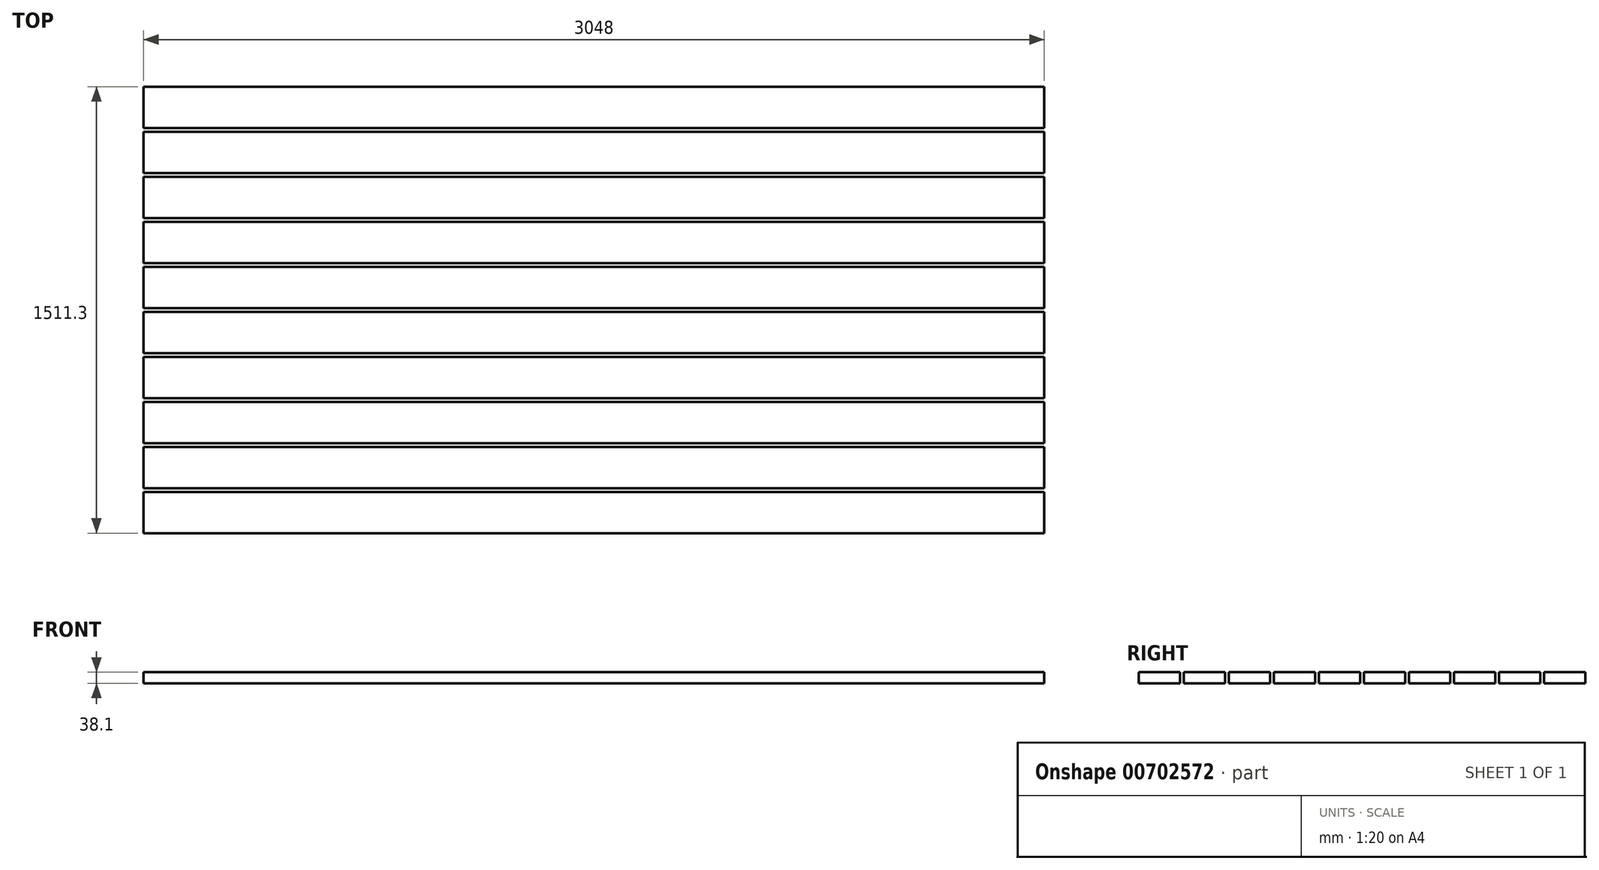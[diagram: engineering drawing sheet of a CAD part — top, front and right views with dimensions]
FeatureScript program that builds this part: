
annotation { "Feature Type Name" : "Feature", "Feature Type Description" : "" }
export const myFeature = defineFeature(function(context is Context, id is Id, definition is map)
    precondition{}
    {
        {
            var Q0;
            Q0=qCreatedBy(makeId("Top.planeOp"),FACE);
            var sketch = newSketch(context, id + "F0", { "sketchPlane" : qUnion([Q0])});
            skLineSegment(sketch, "E0.bottom", {"start": v(1524, 69.85) * mm, "end": v(-1524, 69.85) * mm});
            skLineSegment(sketch, "E0.top", {"start": v(1524, -69.85) * mm, "end": v(-1524, -69.85) * mm});
            skLineSegment(sketch, "E0.left", {"start": v(1524, 69.85) * mm, "end": v(1524, -69.85) * mm});
            skLineSegment(sketch, "E0.right", {"start": v(-1524, 69.85) * mm, "end": v(-1524, -69.85) * mm});
            skPoint(sketch, "E0.middle", {"position": v(0, 0) * mm});
            skLineSegment(sketch, "E1.bottom", {"start": v(-1524, -82.55) * mm, "end": v(1524, -82.55) * mm});
            skLineSegment(sketch, "E1.top", {"start": v(-1524, -222.25) * mm, "end": v(1524, -222.25) * mm});
            skLineSegment(sketch, "E1.left", {"start": v(-1524, -82.55) * mm, "end": v(-1524, -222.25) * mm});
            skLineSegment(sketch, "E1.right", {"start": v(1524, -82.55) * mm, "end": v(1524, -222.25) * mm});
            skLineSegment(sketch, "E2.bottom", {"start": v(-1524, -234.95) * mm, "end": v(1524, -234.95) * mm});
            skLineSegment(sketch, "E2.top", {"start": v(-1524, -374.65) * mm, "end": v(1524, -374.65) * mm});
            skLineSegment(sketch, "E2.left", {"start": v(-1524, -234.95) * mm, "end": v(-1524, -374.65) * mm});
            skLineSegment(sketch, "E2.right", {"start": v(1524, -234.95) * mm, "end": v(1524, -374.65) * mm});
            skLineSegment(sketch, "E3.bottom", {"start": v(-1524, -387.35) * mm, "end": v(1524, -387.35) * mm});
            skLineSegment(sketch, "E3.top", {"start": v(-1524, -527.05) * mm, "end": v(1524, -527.05) * mm});
            skLineSegment(sketch, "E3.left", {"start": v(-1524, -387.35) * mm, "end": v(-1524, -527.05) * mm});
            skLineSegment(sketch, "E3.right", {"start": v(1524, -387.35) * mm, "end": v(1524, -527.05) * mm});
            skLineSegment(sketch, "E4.bottom", {"start": v(-1524, -539.75) * mm, "end": v(1524, -539.75) * mm});
            skLineSegment(sketch, "E4.top", {"start": v(-1524, -679.45) * mm, "end": v(1524, -679.45) * mm});
            skLineSegment(sketch, "E4.left", {"start": v(-1524, -539.75) * mm, "end": v(-1524, -679.45) * mm});
            skLineSegment(sketch, "E4.right", {"start": v(1524, -539.75) * mm, "end": v(1524, -679.45) * mm});
            skLineSegment(sketch, "E5.bottom", {"start": v(-1524, -692.15) * mm, "end": v(1524, -692.15) * mm});
            skLineSegment(sketch, "E5.top", {"start": v(-1524, -831.85) * mm, "end": v(1524, -831.85) * mm});
            skLineSegment(sketch, "E5.left", {"start": v(-1524, -692.15) * mm, "end": v(-1524, -831.85) * mm});
            skLineSegment(sketch, "E5.right", {"start": v(1524, -692.15) * mm, "end": v(1524, -831.85) * mm});
            skLineSegment(sketch, "E6.bottom", {"start": v(-1524, -844.55) * mm, "end": v(1524, -844.55) * mm});
            skLineSegment(sketch, "E6.top", {"start": v(-1524, -984.25) * mm, "end": v(1524, -984.25) * mm});
            skLineSegment(sketch, "E6.left", {"start": v(-1524, -844.55) * mm, "end": v(-1524, -984.25) * mm});
            skLineSegment(sketch, "E6.right", {"start": v(1524, -844.55) * mm, "end": v(1524, -984.25) * mm});
            skLineSegment(sketch, "E7.bottom", {"start": v(-1524, -996.95) * mm, "end": v(1524, -996.95) * mm});
            skLineSegment(sketch, "E7.top", {"start": v(-1524, -1136.65) * mm, "end": v(1524, -1136.65) * mm});
            skLineSegment(sketch, "E7.left", {"start": v(-1524, -996.95) * mm, "end": v(-1524, -1136.65) * mm});
            skLineSegment(sketch, "E7.right", {"start": v(1524, -996.95) * mm, "end": v(1524, -1136.65) * mm});
            skLineSegment(sketch, "E8.bottom", {"start": v(-1524, -1149.35) * mm, "end": v(1524, -1149.35) * mm});
            skLineSegment(sketch, "E8.top", {"start": v(-1524, -1289.05) * mm, "end": v(1524, -1289.05) * mm});
            skLineSegment(sketch, "E8.left", {"start": v(-1524, -1149.35) * mm, "end": v(-1524, -1289.05) * mm});
            skLineSegment(sketch, "E8.right", {"start": v(1524, -1149.35) * mm, "end": v(1524, -1289.05) * mm});
            skLineSegment(sketch, "E9.bottom", {"start": v(-1524, -1301.75) * mm, "end": v(1524, -1301.75) * mm});
            skLineSegment(sketch, "E9.top", {"start": v(-1524, -1441.45) * mm, "end": v(1524, -1441.45) * mm});
            skLineSegment(sketch, "E9.left", {"start": v(-1524, -1301.75) * mm, "end": v(-1524, -1441.45) * mm});
            skLineSegment(sketch, "E9.right", {"start": v(1524, -1301.75) * mm, "end": v(1524, -1441.45) * mm});
            skSolve(sketch);
        }
        {
            var Q0;
            Q0 = qSketchRegion(id + "F0", true);
            extrude(context, id + "F1", {"entities" : qUnion([Q0]), "depth" : 38.1 * mm, "offsetDistance" : 25.4 * mm});
        }
    });
